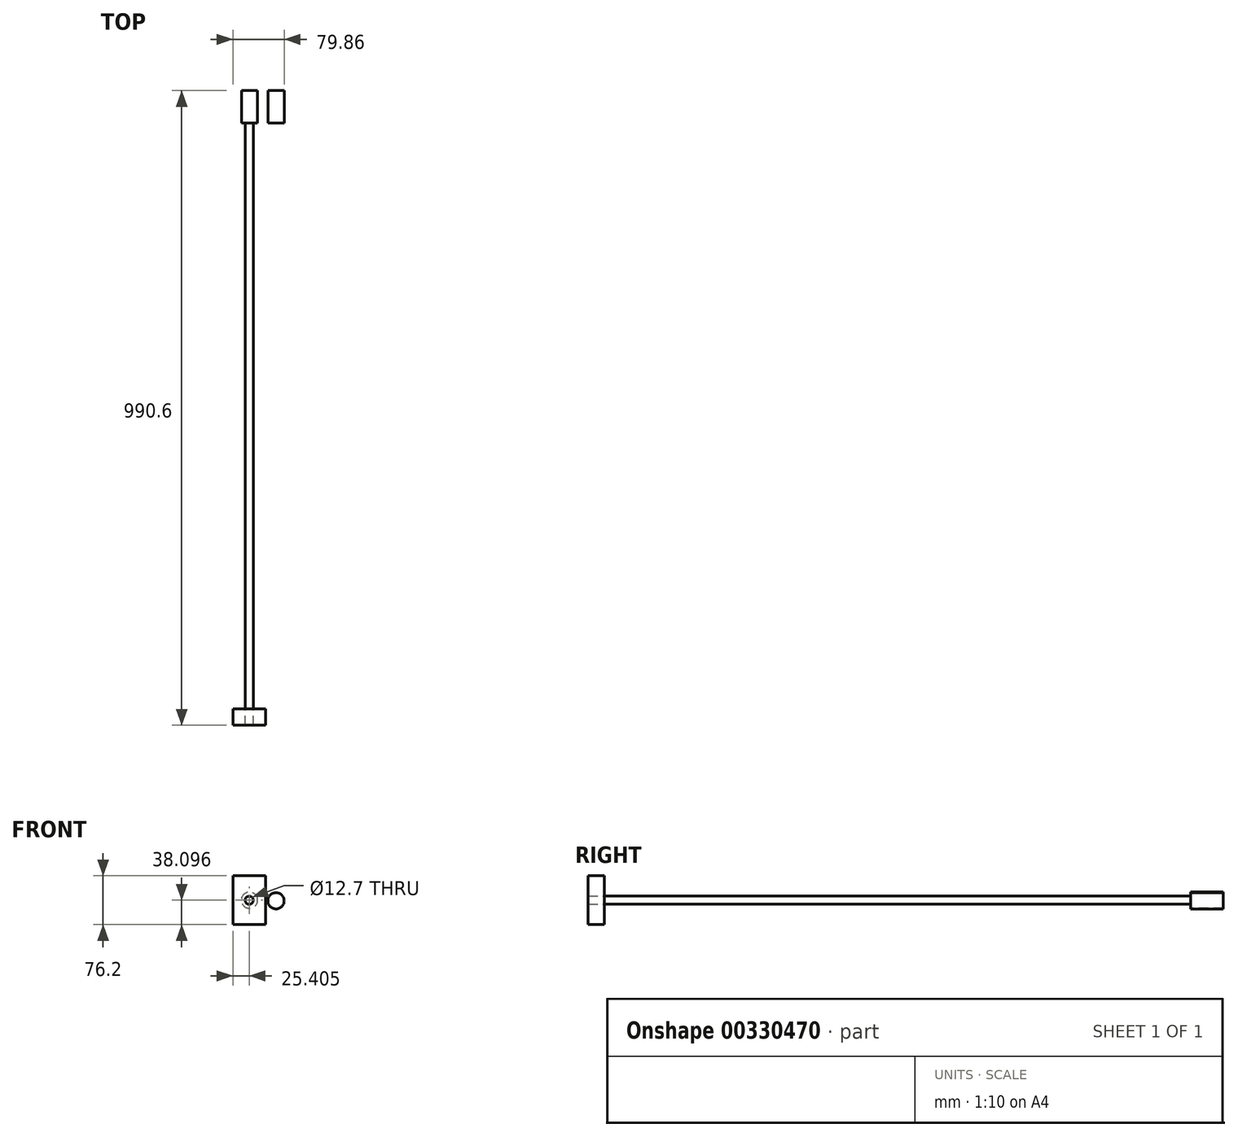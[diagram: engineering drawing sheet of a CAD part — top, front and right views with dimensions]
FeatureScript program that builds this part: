
annotation { "Feature Type Name" : "Feature", "Feature Type Description" : "" }
export const myFeature = defineFeature(function(context is Context, id is Id, definition is map)
    precondition{}
    {
        {
            var Q0;
            Q0=qCreatedBy(makeId("Front.planeOp"),FACE);
            var sketch = newSketch(context, id + "F0", { "sketchPlane" : qUnion([Q0])});
            skCircle(sketch, "E0", {"center": v(-53.95, 47.93) * mm, "radius": 12.7 * mm});
            skCircle(sketch, "E1", {"center": v(-12.64, 46.85) * mm, "radius": 12.7 * mm});
            skSolve(sketch);
        }
        {
            var Q0;
            Q0 = qSketchRegion(id + "F0", true);
            extrude(context, id + "F1", {"entities" : qUnion([Q0]), "oppositeDirection" : true, "depth" : 50.8 * mm});
        }
        {
            var Q0;
            Q0=qCreatedBy(makeId("Front.planeOp"),FACE);
            var sketch = newSketch(context, id + "F2", { "sketchPlane" : qUnion([Q0])});
            skCircle(sketch, "E2", {"center": v(-54.4, 47.78) * mm, "radius": 6.35 * mm});
            skCircle(sketch, "E3", {"center": v(-12.66, 46.62) * mm, "radius": 6.35 * mm});
            skSolve(sketch);
        }
        {
            var Q0;
            Q0 = qSketchRegion(id + "F2", true);
            extrude(context, id + "F3", {"entities" : qUnion([Q0]), "depth" : 914.4 * mm});
        }
        {
            var Q0;
            Q0=makeQuery(id+"F3.opExtrude","CAP_FACE",FACE,{"disambiguationData":[OSD([sQuery(id+"F2.wireOp",EDGE,"E2")])],"isStart":false});
            var sketch = newSketch(context, id + "F4", { "sketchPlane" : qUnion([Q0])});
            skLineSegment(sketch, "E4.bottom", {"start": v(-29, 9.68) * mm, "end": v(-79.8, 9.68) * mm});
            skLineSegment(sketch, "E4.top", {"start": v(-29, 85.88) * mm, "end": v(-79.8, 85.88) * mm});
            skLineSegment(sketch, "E4.left", {"start": v(-29, 9.68) * mm, "end": v(-29, 85.88) * mm});
            skLineSegment(sketch, "E4.right", {"start": v(-79.8, 9.68) * mm, "end": v(-79.8, 85.88) * mm});
            skPoint(sketch, "E4.middle", {"position": v(-54.4, 47.78) * mm});
            skSolve(sketch);
        }
        {
            var Q0;
            Q0=makeQuery(id+"F4.imprint","IMPRINT",FACE,{"disambiguationData":[TD([[makeQuery(id+"F4.imprint","IMPRINT",EDGE,{"derivedFrom":sQuery(id+"F4.wireOp",EDGE,"E4.bottom")}),-1.0]])]});
            extrude(context, id + "F5", {"entities" : qUnion([Q0]), "depth" : 25.4 * mm});
        }
        {
            var Q0;
            Q0=makeQuery(id+"F3.opExtrude","SWEPT_BODY",BODY,{"disambiguationData":[OSD([sQuery(id+"F2.wireOp",EDGE,"E3")])]});
            deleteBodies(context, id + "F6", {"entities" : qUnion([Q0])});
        }
    });
